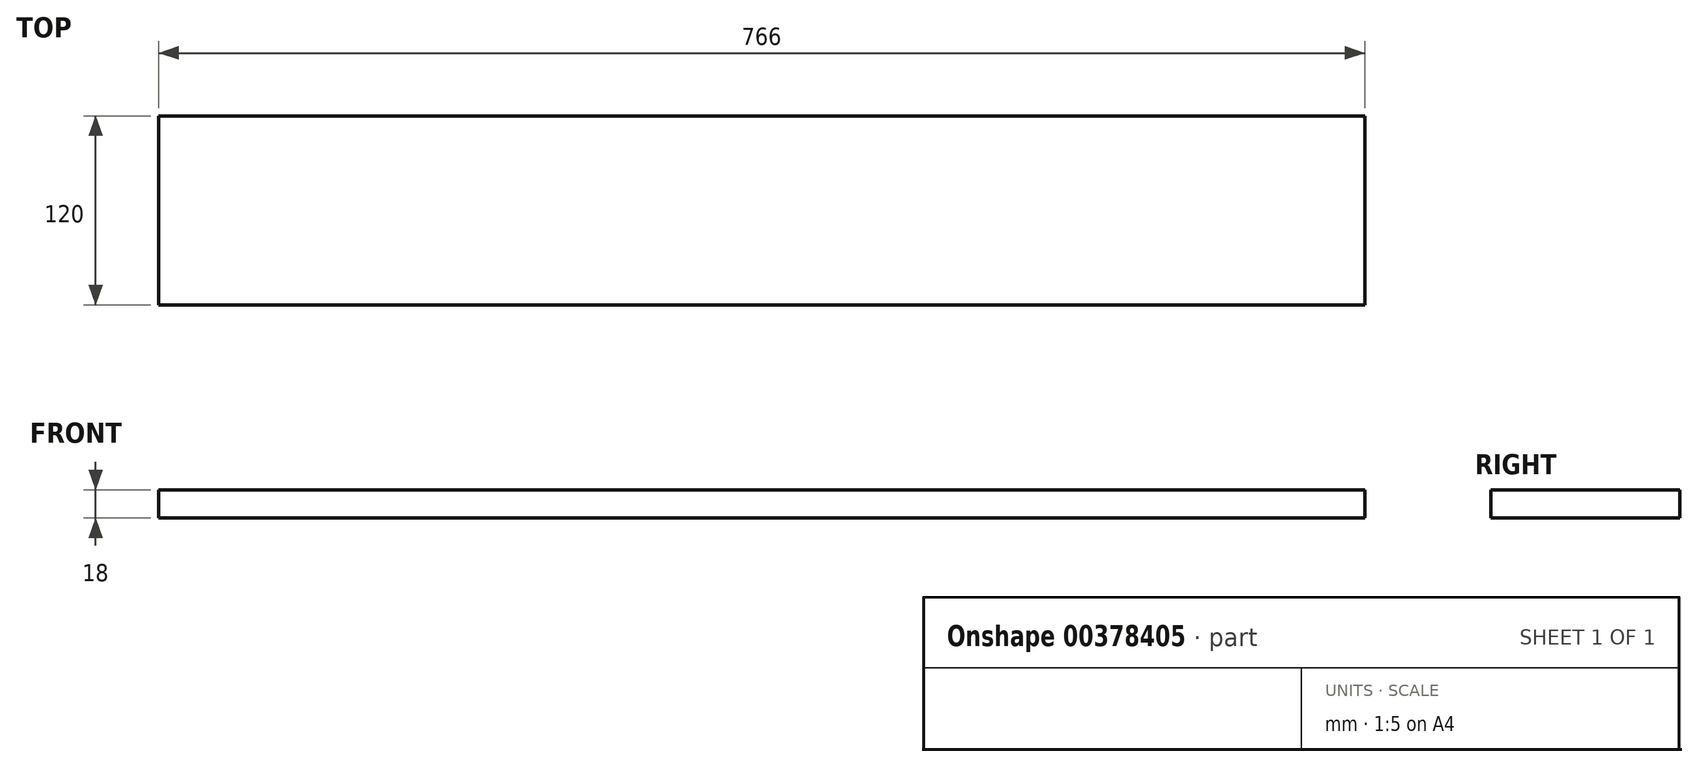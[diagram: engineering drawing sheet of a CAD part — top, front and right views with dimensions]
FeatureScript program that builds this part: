
annotation { "Feature Type Name" : "Feature", "Feature Type Description" : "" }
export const myFeature = defineFeature(function(context is Context, id is Id, definition is map)
    precondition{}
    {
        {
            var Q0;
            Q0=qCreatedBy(makeId("Right.planeOp"),FACE);
            var sketch = newSketch(context, id + "F0", { "sketchPlane" : qUnion([Q0])});
            skLineSegment(sketch, "E0.bottom", {"start": v(60, 9) * mm, "end": v(-60, 9) * mm});
            skLineSegment(sketch, "E0.top", {"start": v(60, -9) * mm, "end": v(-60, -9) * mm});
            skLineSegment(sketch, "E0.left", {"start": v(60, 9) * mm, "end": v(60, -9) * mm});
            skLineSegment(sketch, "E0.right", {"start": v(-60, 9) * mm, "end": v(-60, -9) * mm});
            skPoint(sketch, "E0.middle", {"position": v(0, 0) * mm});
            skSolve(sketch);
        }
        {
            var Q0;
            Q0 = qSketchRegion(id + "F0", true);
            extrude(context, id + "F1", {"entities" : qUnion([Q0]), "depth" : 766 * mm});
        }
    });
